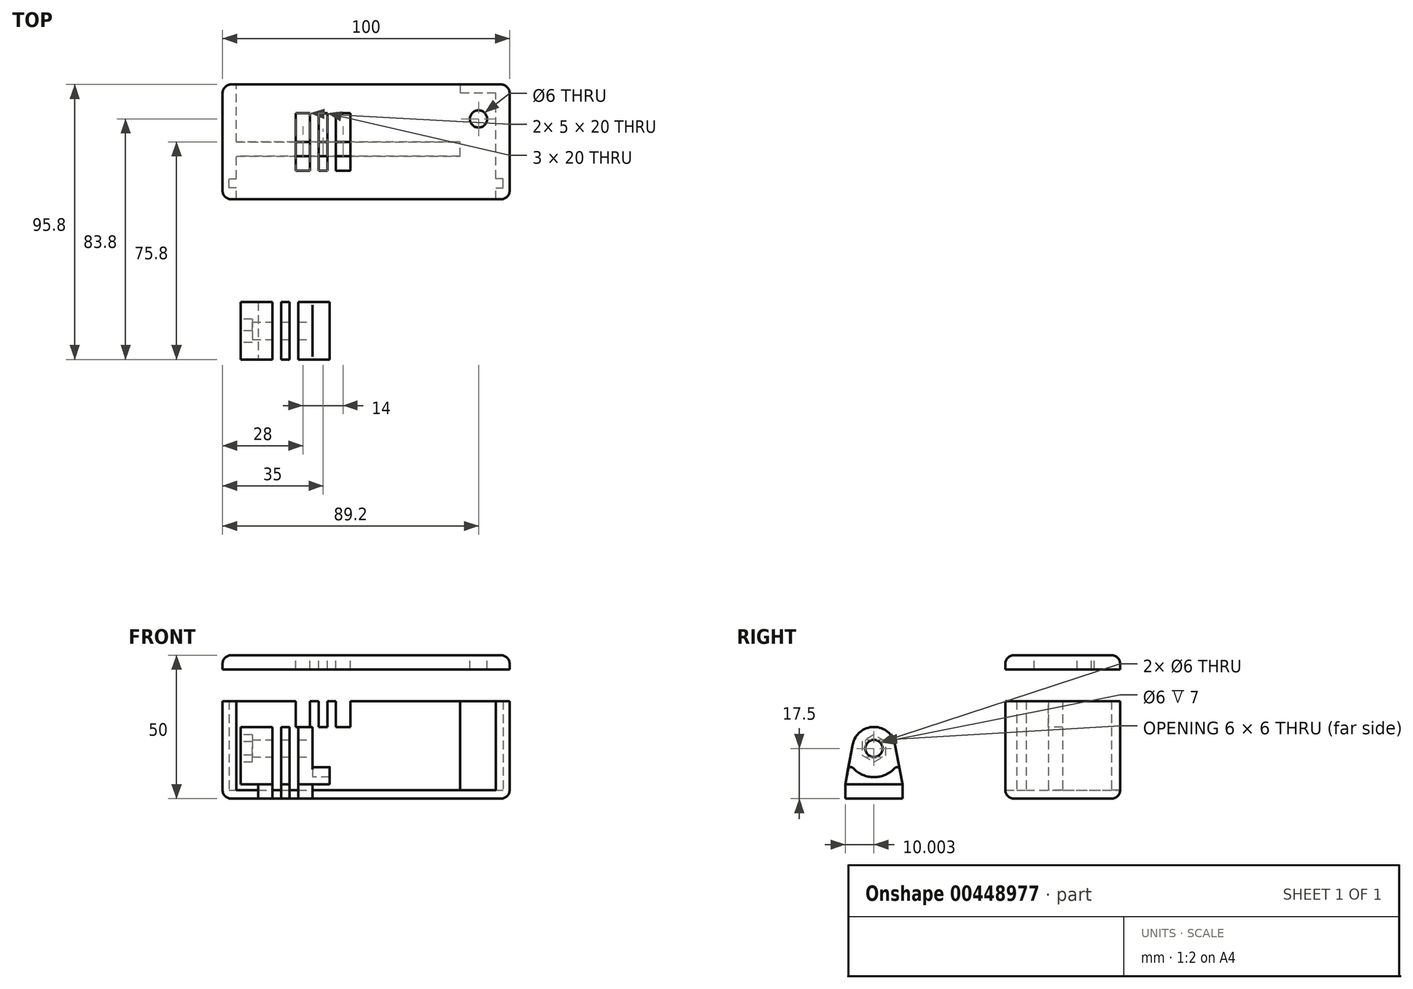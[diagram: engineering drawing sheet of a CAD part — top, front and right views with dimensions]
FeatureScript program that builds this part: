
annotation { "Feature Type Name" : "Feature", "Feature Type Description" : "" }
export const myFeature = defineFeature(function(context is Context, id is Id, definition is map)
    precondition{}
    {
        {
            var Q0;
            Q0=qCreatedBy(makeId("Top.planeOp"),FACE);
            var sketch = newSketch(context, id + "F0", { "sketchPlane" : qUnion([Q0])});
            skLineSegment(sketch, "E0.bottom", {"start": v(0, 0) * mm, "end": v(100, 0) * mm});
            skLineSegment(sketch, "E0.top", {"start": v(0, 40) * mm, "end": v(100, 40) * mm});
            skLineSegment(sketch, "E0.left", {"start": v(0, 0) * mm, "end": v(0, 40) * mm});
            skLineSegment(sketch, "E0.right", {"start": v(100, 0) * mm, "end": v(100, 40) * mm});
            skLineSegment(sketch, "E1", {"start": v(4.8, 37) * mm, "end": v(4.8, 20) * mm});
            skLineSegment(sketch, "E2", {"start": v(4.8, 7.2) * mm, "end": v(2.3, 7.2) * mm});
            skLineSegment(sketch, "E3", {"start": v(2.3, 7.2) * mm, "end": v(2.3, 4) * mm});
            skLineSegment(sketch, "E4", {"start": v(2.3, 4) * mm, "end": v(4.8, 4) * mm});
            skLineSegment(sketch, "E5", {"start": v(4.8, 4) * mm, "end": v(4.8, 0) * mm});
            skLineSegment(sketch, "E6", {"start": v(95.2, 37) * mm, "end": v(95.2, 7.2) * mm});
            skLineSegment(sketch, "E7", {"start": v(95.2, 7.2) * mm, "end": v(97.7, 7.2) * mm});
            skLineSegment(sketch, "E8", {"start": v(97.7, 7.2) * mm, "end": v(97.7, 4) * mm});
            skLineSegment(sketch, "E9", {"start": v(97.7, 4) * mm, "end": v(95.2, 4) * mm});
            skLineSegment(sketch, "E10", {"start": v(95.2, 4) * mm, "end": v(95.2, 0) * mm});
            skLineSegment(sketch, "E11", {"start": v(82.8, 37) * mm, "end": v(95.2, 37) * mm});
            skLineSegment(sketch, "E12", {"start": v(4.8, 37) * mm, "end": v(4.8, 40) * mm});
            skLineSegment(sketch, "E13", {"start": v(82.8, 37) * mm, "end": v(82.8, 40) * mm});
            skLineSegment(sketch, "E14", {"start": v(4.8, 15) * mm, "end": v(82.8, 15) * mm});
            skLineSegment(sketch, "E15", {"start": v(82.8, 15) * mm, "end": v(82.8, 20) * mm});
            skLineSegment(sketch, "E16", {"start": v(82.8, 20) * mm, "end": v(4.8, 20) * mm});
            skLineSegment(sketch, "E17.trimOffspring", {"start": v(4.8, 15) * mm, "end": v(4.8, 7.2) * mm});
            skSolve(sketch);
        }
        {
            var Q0;
            {var subQ1=sQuery(id+"F0.wireOp",EDGE,"E0.left");Q0=makeQuery(id+"F0.imprint","IMPRINT",FACE,{"disambiguationData":[TD([[makeQuery(id+"F0.imprint","IMPRINT",EDGE,{"derivedFrom":subQ1}),-1.0]])]});}
            var Q1;
            {var subQ0=sQuery(id+"F0.wireOp",EDGE,"E0.right");Q1=makeQuery(id+"F0.imprint","IMPRINT",FACE,{"disambiguationData":[TD([[makeQuery(id+"F0.imprint","IMPRINT",EDGE,{"derivedFrom":subQ0}),1.0]])]});}
            var Q2;
            Q2=makeQuery(id+"F0.imprint","IMPRINT",FACE,{"disambiguationData":[TD([[makeQuery(id+"F0.imprint","IMPRINT",EDGE,{"derivedFrom":sQuery(id+"F0.wireOp",EDGE,"E1")}),1.0]])]});
            extrude(context, id + "F1", {"entities" : qUnion([Q0, Q1, Q2]), "depth" : 3 * mm});
        }
        {
            var Q0;
            {var subQ1=sQuery(id+"F0.wireOp",EDGE,"E0.left");Q0=makeQuery(id+"F0.imprint","IMPRINT",FACE,{"disambiguationData":[TD([[makeQuery(id+"F0.imprint","IMPRINT",EDGE,{"derivedFrom":subQ1}),-1.0]])]});}
            var Q1;
            {var subQ0=sQuery(id+"F0.wireOp",EDGE,"E0.right");Q1=makeQuery(id+"F0.imprint","IMPRINT",FACE,{"disambiguationData":[TD([[makeQuery(id+"F0.imprint","IMPRINT",EDGE,{"derivedFrom":subQ0}),1.0]])]});}
            extrude(context, id + "F2", {"entities" : qUnion([Q0, Q1]), "operationType" : NewBodyOperationType.ADD, "depth" : 34 * mm});
        }
        {
            var Q0;
            Q0=makeQuery(id+"F1.opExtrude","CAP_EDGE",EDGE,{"disambiguationData":[OSD([sQuery(id+"F0.wireOp",EDGE,"E0.right")])],"isStart":true});
            var Q1;
            Q1=makeQuery(id+"F1.opExtrude","CAP_EDGE",EDGE,{"disambiguationData":[OSD([sQuery(id+"F0.wireOp",EDGE,"E0.bottom")])],"isStart":true});
            var Q2;
            {var subQ0=sQuery(id+"F0.wireOp",EDGE,"E0.right");var subQ1=sQuery(id+"F0.wireOp",EDGE,"E0.bottom");Q2=makeQuery(id+"F2.boolean.opBoolean","MERGE",EDGE,{"derivedFrom":[makeQuery(id+"F1.opExtrude","SWEPT_EDGE",EDGE,{"disambiguationData":[OSD([subQ1,subQ0])]}),makeQuery(id+"F2.opExtrude","SWEPT_EDGE",EDGE,{"disambiguationData":[OSD([subQ1,subQ0])]})]});}
            var Q3;
            Q3=makeQuery(id+"F1.opExtrude","CAP_EDGE",EDGE,{"disambiguationData":[OSD([sQuery(id+"F0.wireOp",EDGE,"E0.left")])],"isStart":true});
            var Q4;
            {var subQ0=sQuery(id+"F0.wireOp",EDGE,"E0.left");var subQ1=sQuery(id+"F0.wireOp",EDGE,"E0.bottom");Q4=makeQuery(id+"F2.boolean.opBoolean","MERGE",EDGE,{"derivedFrom":[makeQuery(id+"F1.opExtrude","SWEPT_EDGE",EDGE,{"disambiguationData":[OSD([subQ1,subQ0])]}),makeQuery(id+"F2.opExtrude","SWEPT_EDGE",EDGE,{"disambiguationData":[OSD([subQ1,subQ0])]})]});}
            var Q5;
            {var subQ0=sQuery(id+"F0.wireOp",EDGE,"E0.left");var subQ1=sQuery(id+"F0.wireOp",EDGE,"E0.top");Q5=makeQuery(id+"F2.boolean.opBoolean","MERGE",EDGE,{"derivedFrom":[makeQuery(id+"F1.opExtrude","SWEPT_EDGE",EDGE,{"disambiguationData":[OSD([subQ1,subQ0])]}),makeQuery(id+"F2.opExtrude","SWEPT_EDGE",EDGE,{"disambiguationData":[OSD([subQ1,subQ0])]})]});}
            var Q6;
            {var subQ0=sQuery(id+"F0.wireOp",EDGE,"E0.right");var subQ1=sQuery(id+"F0.wireOp",EDGE,"E0.top");Q6=makeQuery(id+"F2.boolean.opBoolean","MERGE",EDGE,{"derivedFrom":[makeQuery(id+"F1.opExtrude","SWEPT_EDGE",EDGE,{"disambiguationData":[OSD([subQ1,subQ0])]}),makeQuery(id+"F2.opExtrude","SWEPT_EDGE",EDGE,{"disambiguationData":[OSD([subQ1,subQ0])]})]});}
            var Q7;
            Q7=makeQuery(id+"F1.opExtrude","CAP_EDGE",EDGE,{"disambiguationData":[OSD([sQuery(id+"F0.wireOp",EDGE,"E0.top")])],"isStart":true});
            fillet(context, id + "F3", {"entities" : qUnion([Q0, Q1, Q2, Q3, Q4, Q5, Q6, Q7]), "radius" : 3 * mm, "tangentPropagation" : true, "allowEdgeOverflow" : false});
        }
        {
            var Q0;
            Q0=makeQuery(id+"F0.imprint","IMPRINT",FACE,{"disambiguationData":[TD([[makeQuery(id+"F0.imprint","IMPRINT",EDGE,{"derivedFrom":sQuery(id+"F0.wireOp",EDGE,"E1")}),1.0]])]});
            var Q1;
            {var subQ1=sQuery(id+"F0.wireOp",EDGE,"E0.left");Q1=makeQuery(id+"F0.imprint","IMPRINT",FACE,{"disambiguationData":[TD([[makeQuery(id+"F0.imprint","IMPRINT",EDGE,{"derivedFrom":subQ1}),-1.0]])]});}
            var Q2;
            {var subQ0=sQuery(id+"F0.wireOp",EDGE,"E0.right");Q2=makeQuery(id+"F0.imprint","IMPRINT",FACE,{"disambiguationData":[TD([[makeQuery(id+"F0.imprint","IMPRINT",EDGE,{"derivedFrom":subQ0}),1.0]])]});}
            extrude(context, id + "F4", {"entities" : qUnion([Q0, Q1, Q2]), "depth" : 50 * mm, "hasSecondDirection" : true, "secondDirectionOppositeDirection" : false, "secondDirectionDepth" : 45 * mm});
        }
        {
            var Q0;
            Q0=makeQuery(id+"F4.opExtrude","CAP_FACE",FACE,{"disambiguationData":[OSD([sQuery(id+"F0.wireOp",EDGE,"E0.bottom"),sQuery(id+"F0.wireOp",EDGE,"E0.top"),sQuery(id+"F0.wireOp",EDGE,"E0.left"),sQuery(id+"F0.wireOp",EDGE,"E0.right")])],"isStart":false});
            var sketch = newSketch(context, id + "F5", { "sketchPlane" : qUnion([Q0])});
            skLineSegment(sketch, "E18.bottom", {"start": v(22.5, 30) * mm, "end": v(47.5, 30) * mm, "construction": true});
            skLineSegment(sketch, "E18.top", {"start": v(22.5, 10) * mm, "end": v(47.5, 10) * mm, "construction": true});
            skLineSegment(sketch, "E18.left", {"start": v(22.5, 30) * mm, "end": v(22.5, 10) * mm, "construction": true});
            skLineSegment(sketch, "E18.right", {"start": v(47.5, 30) * mm, "end": v(47.5, 10) * mm, "construction": true});
            skPoint(sketch, "E19", {"position": v(35, 20) * mm});
            skPoint(sketch, "E19.positionSnap0", {"position": v(22.5, 20) * mm});
            skPoint(sketch, "E19.positionSnap1", {"position": v(35, 30) * mm});
            skLineSegment(sketch, "E20.bottom", {"start": v(33.5, 30) * mm, "end": v(36.5, 30) * mm});
            skLineSegment(sketch, "E20.top", {"start": v(33.5, 10) * mm, "end": v(36.5, 10) * mm});
            skLineSegment(sketch, "E20.left", {"start": v(33.5, 30) * mm, "end": v(33.5, 10) * mm});
            skLineSegment(sketch, "E20.right", {"start": v(36.5, 30) * mm, "end": v(36.5, 10) * mm});
            skLineSegment(sketch, "E21.bottom", {"start": v(30.5, 30) * mm, "end": v(25.5, 30) * mm});
            skLineSegment(sketch, "E21.top", {"start": v(30.5, 10) * mm, "end": v(25.5, 10) * mm});
            skLineSegment(sketch, "E21.left", {"start": v(30.5, 30) * mm, "end": v(30.5, 10) * mm});
            skLineSegment(sketch, "E21.right", {"start": v(25.5, 30) * mm, "end": v(25.5, 10) * mm});
            skLineSegment(sketch, "E22.bottom", {"start": v(39.5, 30) * mm, "end": v(44.5, 30) * mm});
            skLineSegment(sketch, "E22.top", {"start": v(39.5, 10) * mm, "end": v(44.5, 10) * mm});
            skLineSegment(sketch, "E22.left", {"start": v(39.5, 30) * mm, "end": v(39.5, 10) * mm});
            skLineSegment(sketch, "E22.right", {"start": v(44.5, 30) * mm, "end": v(44.5, 10) * mm});
            skPoint(sketch, "E23", {"position": v(33.5, 20) * mm});
            skPoint(sketch, "E24", {"position": v(36.5, 20) * mm});
            skPoint(sketch, "E25", {"position": v(35, 10) * mm});
            skCircle(sketch, "E26", {"center": v(89.2, 28) * mm, "radius": 3 * mm});
            skSolve(sketch);
        }
        {
            var Q0;
            Q0 = qSketchRegion(id + "F5", true);
            extrude(context, id + "F6", {"entities" : qUnion([Q0]), "operationType" : NewBodyOperationType.REMOVE, "oppositeDirection" : true, "depth" : 25 * mm});
        }
        {
            var Q0;
            Q0=makeQuery(id+"F4.opExtrude","SWEPT_EDGE",EDGE,{"disambiguationData":[OSD([sQuery(id+"F0.wireOp",EDGE,"E0.bottom"),sQuery(id+"F0.wireOp",EDGE,"E0.left")])]});
            var Q1;
            Q1=makeQuery(id+"F4.opExtrude","SWEPT_EDGE",EDGE,{"disambiguationData":[OSD([sQuery(id+"F0.wireOp",EDGE,"E0.top"),sQuery(id+"F0.wireOp",EDGE,"E0.left")])]});
            var Q2;
            Q2=makeQuery(id+"F4.opExtrude","SWEPT_EDGE",EDGE,{"disambiguationData":[OSD([sQuery(id+"F0.wireOp",EDGE,"E0.bottom"),sQuery(id+"F0.wireOp",EDGE,"E0.right")])]});
            var Q3;
            Q3=makeQuery(id+"F4.opExtrude","SWEPT_EDGE",EDGE,{"disambiguationData":[OSD([sQuery(id+"F0.wireOp",EDGE,"E0.top"),sQuery(id+"F0.wireOp",EDGE,"E0.right")])]});
            var Q4;
            Q4=makeQuery(id+"F4.opExtrude","CAP_EDGE",EDGE,{"disambiguationData":[OSD([sQuery(id+"F0.wireOp",EDGE,"E0.bottom")])],"isStart":false});
            var Q5;
            Q5=makeQuery(id+"F4.opExtrude","CAP_EDGE",EDGE,{"disambiguationData":[OSD([sQuery(id+"F0.wireOp",EDGE,"E0.left")])],"isStart":false});
            var Q6;
            Q6=makeQuery(id+"F4.opExtrude","CAP_EDGE",EDGE,{"disambiguationData":[OSD([sQuery(id+"F0.wireOp",EDGE,"E0.top")])],"isStart":false});
            var Q7;
            Q7=makeQuery(id+"F4.opExtrude","CAP_EDGE",EDGE,{"disambiguationData":[OSD([sQuery(id+"F0.wireOp",EDGE,"E0.right")])],"isStart":false});
            fillet(context, id + "F7", {"entities" : qUnion([Q0, Q1, Q2, Q3, Q4, Q5, Q6, Q7]), "radius" : 3 * mm, "tangentPropagation" : true, "allowEdgeOverflow" : false});
        }
        {
            var Q0;
            Q0=qCreatedBy(makeId("Top.planeOp"),FACE);
            var sketch = newSketch(context, id + "F8", { "sketchPlane" : qUnion([Q0])});
            skLineSegment(sketch, "E27.bottom", {"start": v(12.35, -35.8) * mm, "end": v(31.35, -35.8) * mm});
            skLineSegment(sketch, "E27.top", {"start": v(12.35, -55.8) * mm, "end": v(31.35, -55.8) * mm});
            skLineSegment(sketch, "E27.left", {"start": v(12.35, -35.8) * mm, "end": v(12.35, -55.8) * mm});
            skLineSegment(sketch, "E27.right", {"start": v(31.35, -35.8) * mm, "end": v(31.35, -55.8) * mm});
            skLineSegment(sketch, "E28", {"start": v(17.35, -35.8) * mm, "end": v(17.35, -55.8) * mm});
            skLineSegment(sketch, "E29", {"start": v(17.35, -55.8) * mm, "end": v(20.35, -55.8) * mm});
            skLineSegment(sketch, "E30", {"start": v(20.35, -55.8) * mm, "end": v(20.35, -35.8) * mm});
            skLineSegment(sketch, "E31", {"start": v(20.35, -35.8) * mm, "end": v(23.35, -35.8) * mm});
            skLineSegment(sketch, "E32", {"start": v(23.35, -35.8) * mm, "end": v(23.35, -55.8) * mm});
            skLineSegment(sketch, "E33", {"start": v(23.35, -55.8) * mm, "end": v(26.35, -55.8) * mm});
            skLineSegment(sketch, "E34", {"start": v(26.35, -55.8) * mm, "end": v(26.35, -35.8) * mm});
            skSolve(sketch);
        }
        {
            var Q0;
            {var subQ0=sQuery(id+"F8.wireOp",EDGE,"E27.left");Q0=makeQuery(id+"F8.imprint","IMPRINT",FACE,{"disambiguationData":[TD([[makeQuery(id+"F8.imprint","IMPRINT",EDGE,{"derivedFrom":subQ0}),1.0]])]});}
            var Q1;
            {var subQ0=sQuery(id+"F8.wireOp",EDGE,"E27.right");Q1=makeQuery(id+"F8.imprint","IMPRINT",FACE,{"disambiguationData":[TD([[makeQuery(id+"F8.imprint","IMPRINT",EDGE,{"derivedFrom":subQ0}),-1.0]])]});}
            var Q2;
            {var subQ0=sQuery(id+"F8.wireOp",EDGE,"E30");Q2=makeQuery(id+"F8.imprint","IMPRINT",FACE,{"disambiguationData":[TD([[makeQuery(id+"F8.imprint","IMPRINT",EDGE,{"derivedFrom":subQ0}),-1.0]])]});}
            extrude(context, id + "F9", {"entities" : qUnion([Q0, Q1, Q2]), "depth" : 25 * mm});
        }
        {
            var Q0;
            Q0=makeQuery(id+"F9.opExtrude","SWEPT_FACE",FACE,{"disambiguationData":[OSD([sQuery(id+"F8.wireOp",EDGE,"E27.right")])]});
            var sketch = newSketch(context, id + "F10", { "sketchPlane" : qUnion([Q0])});
            skCircle(sketch, "E35", {"center": v(-45.8, 17.5) * mm, "radius": 7.5 * mm});
            skLineSegment(sketch, "E36", {"start": v(-55.8, 5) * mm, "end": v(-53.17, 18.9) * mm});
            skLineSegment(sketch, "E37", {"start": v(-35.8, 5) * mm, "end": v(-38.43, 18.9) * mm});
            skCircle(sketch, "E38", {"center": v(-45.8, 17.5) * mm, "radius": 3 * mm});
            skSolve(sketch);
        }
        {
            var Q0;
            {var subQ0=sQuery(id+"F10.wireOp",EDGE,"E36");Q0=makeQuery(id+"F10.imprint","IMPRINT",FACE,{"disambiguationData":[TD([[makeQuery(id+"F10.imprint","IMPRINT",EDGE,{"derivedFrom":subQ0}),1.0]])]});}
            var Q1;
            {var subQ0=sQuery(id+"F10.wireOp",EDGE,"E37");Q1=makeQuery(id+"F10.imprint","IMPRINT",FACE,{"disambiguationData":[TD([[makeQuery(id+"F10.imprint","IMPRINT",EDGE,{"derivedFrom":subQ0}),-1.0]])]});}
            var Q2;
            Q2=makeQuery(id+"F10.imprint","IMPRINT",FACE,{"disambiguationData":[TD([[makeQuery(id+"F10.imprint","IMPRINT",EDGE,{"derivedFrom":sQuery(id+"F10.wireOp",EDGE,"E38")}),1.0]])]});
            extrude(context, id + "F11", {"entities" : qUnion([Q0, Q1, Q2]), "operationType" : NewBodyOperationType.REMOVE, "oppositeDirection" : true, "depth" : 25 * mm});
        }
        {
            var Q0;
            Q0=makeQuery(id+"F9.opExtrude","SWEPT_FACE",FACE,{"disambiguationData":[OSD([sQuery(id+"F8.wireOp",EDGE,"E27.right")])]});
            var sketch = newSketch(context, id + "F12", { "sketchPlane" : qUnion([Q0])});
            skLineSegment(sketch, "E39", {"start": v(-55.8, 5) * mm, "end": v(-35.8, 5) * mm});
            skLineSegment(sketch, "E40", {"start": v(-35.8, 5) * mm, "end": v(-37.2, 12.4) * mm});
            skLineSegment(sketch, "E41", {"start": v(-55.8, 5) * mm, "end": v(-54.4, 12.4) * mm});
            skArc(sketch, "E42", {"start": v(-54.4, 12.4) * mm, "mid": v(-45.8, 7.5) * mm, "end": v(-37.2, 12.4) * mm});
            skSolve(sketch);
        }
        {
            var Q0;
            Q0=makeQuery(id+"F12.imprint","IMPRINT",FACE,{"disambiguationData":[TD([[makeQuery(id+"F12.imprint","IMPRINT",EDGE,{"derivedFrom":sQuery(id+"F12.wireOp",EDGE,"E39")}),1.0]])]});
            extrude(context, id + "F13", {"entities" : qUnion([Q0]), "operationType" : NewBodyOperationType.ADD, "depth" : 6 * mm});
        }
        {
            var Q0;
            Q0=makeQuery(id+"F13.opExtrude","SWEPT_EDGE",EDGE,{"disambiguationData":[OSD([sQuery(id+"F10.wireOp",EDGE,"E36"),sQuery(id+"F12.wireOp",EDGE,"E41"),sQuery(id+"F12.wireOp",EDGE,"E42")])]});
            var Q1;
            Q1=makeQuery(id+"F13.opExtrude","SWEPT_EDGE",EDGE,{"disambiguationData":[OSD([sQuery(id+"F10.wireOp",EDGE,"E37"),sQuery(id+"F12.wireOp",EDGE,"E40"),sQuery(id+"F12.wireOp",EDGE,"E42")])]});
            fillet(context, id + "F14", {"entities" : qUnion([Q0, Q1]), "radius" : 1 * mm, "tangentPropagation" : true, "allowEdgeOverflow" : false});
        }
        {
            var Q0;
            Q0=makeQuery(id+"F9.opExtrude","SWEPT_FACE",FACE,{"disambiguationData":[OSD([sQuery(id+"F8.wireOp",EDGE,"E27.left")])]});
            var sketch = newSketch(context, id + "F15", { "sketchPlane" : qUnion([Q0])});
            skLineSegment(sketch, "E43", {"start": v(35.8, 5) * mm, "end": v(55.8, 5) * mm});
            skLineSegment(sketch, "E44", {"start": v(55.8, 5) * mm, "end": v(53.17, 18.9) * mm});
            skLineSegment(sketch, "E45", {"start": v(35.8, 5) * mm, "end": v(38.43, 18.9) * mm});
            skArc(sketch, "E46", {"start": v(53.17, 18.9) * mm, "mid": v(45.8, 25) * mm, "end": v(38.43, 18.9) * mm});
            skCircle(sketch, "E47", {"center": v(45.8, 17.5) * mm, "radius": 3 * mm});
            skSolve(sketch);
        }
        {
            var Q0;
            Q0 = qSketchRegion(id + "F15", true);
            extrude(context, id + "F16", {"entities" : qUnion([Q0]), "operationType" : NewBodyOperationType.ADD, "depth" : 6 * mm});
        }
        {
            var Q0;
            Q0=makeQuery(id+"F16.opExtrude","CAP_FACE",FACE,{"disambiguationData":[OSD([sQuery(id+"F15.wireOp",EDGE,"E43"),sQuery(id+"F15.wireOp",EDGE,"E44"),sQuery(id+"F15.wireOp",EDGE,"E45"),sQuery(id+"F15.wireOp",EDGE,"E46"),sQuery(id+"F15.wireOp",EDGE,"E47")])],"isStart":false});
            var sketch = newSketch(context, id + "F17", { "sketchPlane" : qUnion([Q0])});
            skCircle(sketch, "E48.cCircle", {"center": v(45.8, 17.5) * mm, "radius": 4.1 * mm, "construction": true});
            skLineSegment(sketch, "E48.0", {"start": v(45.8, 22.23) * mm, "end": v(49.9, 19.87) * mm});
            skLineSegment(sketch, "E48.1", {"start": v(49.9, 19.87) * mm, "end": v(49.9, 15.13) * mm});
            skLineSegment(sketch, "E48.2", {"start": v(49.9, 15.13) * mm, "end": v(45.8, 12.77) * mm});
            skLineSegment(sketch, "E48.3", {"start": v(45.8, 12.77) * mm, "end": v(41.7, 15.13) * mm});
            skLineSegment(sketch, "E48.4", {"start": v(41.7, 15.13) * mm, "end": v(41.7, 19.87) * mm});
            skLineSegment(sketch, "E48.5", {"start": v(41.7, 19.87) * mm, "end": v(45.8, 22.23) * mm});
            skPoint(sketch, "E48.0.midPoint", {"position": v(47.85, 21.05) * mm});
            skSolve(sketch);
        }
        {
            var Q0;
            Q0 = qSketchRegion(id + "F17", true);
            extrude(context, id + "F18", {"entities" : qUnion([Q0]), "operationType" : NewBodyOperationType.REMOVE, "oppositeDirection" : true, "depth" : 4 * mm});
        }
    });
